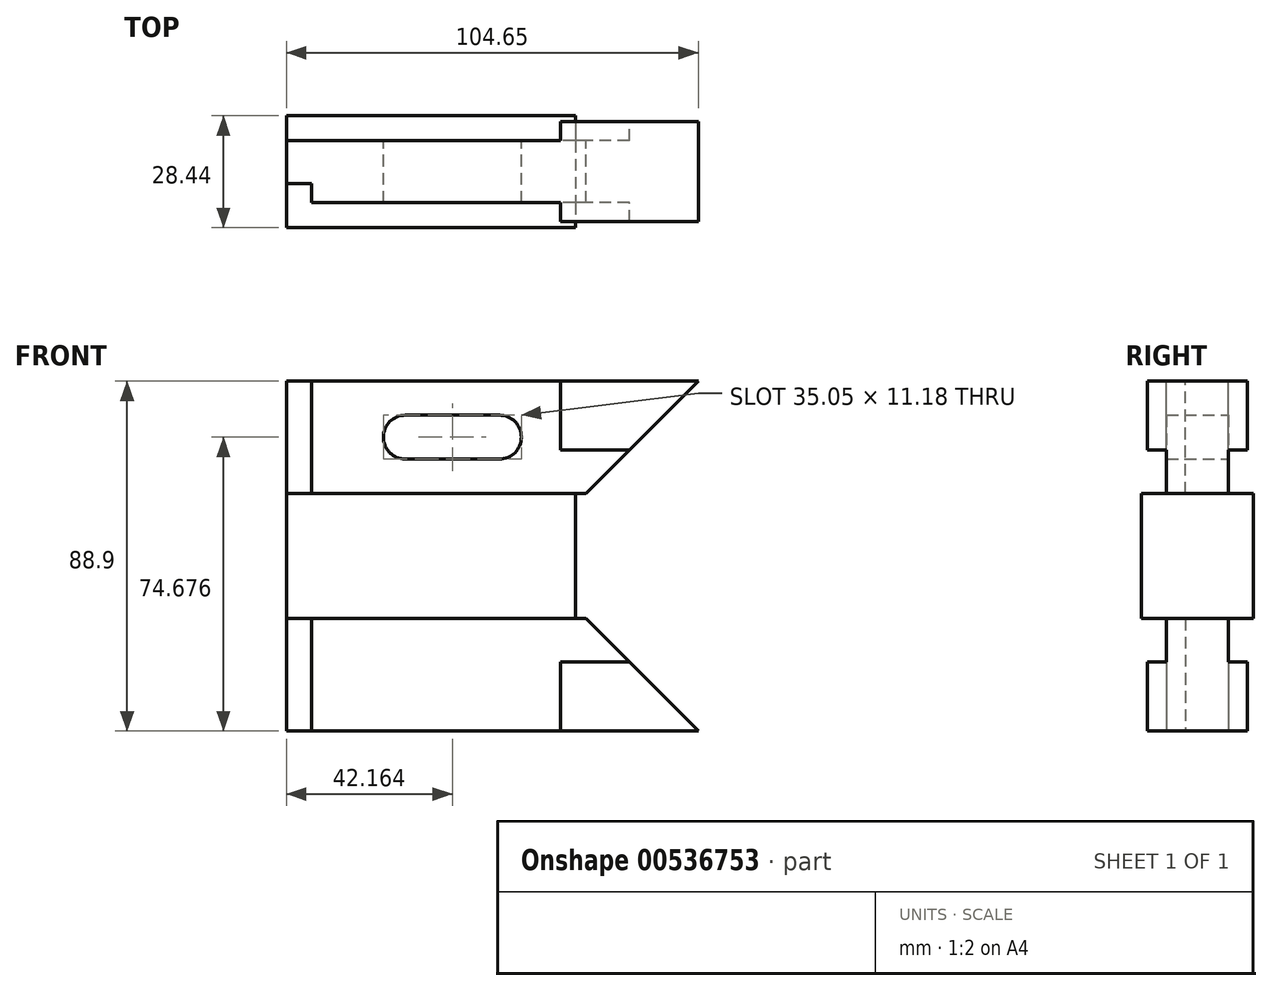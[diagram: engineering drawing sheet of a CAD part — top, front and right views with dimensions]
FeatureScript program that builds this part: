
annotation { "Feature Type Name" : "Feature", "Feature Type Description" : "" }
export const myFeature = defineFeature(function(context is Context, id is Id, definition is map)
    precondition{}
    {
        {
            var Q0;
            Q0=qCreatedBy(makeId("Right.planeOp"),FACE);
            var sketch = newSketch(context, id + "F0", { "sketchPlane" : qUnion([Q0])});
            skLineSegment(sketch, "E0.bottom", {"start": v(14.22, 15.88) * mm, "end": v(-14.22, 15.87) * mm});
            skLineSegment(sketch, "E0.top", {"start": v(14.22, -15.88) * mm, "end": v(-14.22, -15.88) * mm});
            skLineSegment(sketch, "E0.left", {"start": v(14.22, 15.88) * mm, "end": v(14.22, -15.88) * mm});
            skLineSegment(sketch, "E0.right", {"start": v(-14.22, 15.87) * mm, "end": v(-14.22, -15.88) * mm});
            skPoint(sketch, "E0.middle", {"position": v(0, 0) * mm});
            skSolve(sketch);
        }
        {
            var Q0;
            Q0=makeQuery(id+"F0.imprint","IMPRINT",FACE,{"disambiguationData":[TD([[makeQuery(id+"F0.imprint","IMPRINT",EDGE,{"derivedFrom":sQuery(id+"F0.wireOp",EDGE,"E0.bottom")}),1.0]])]});
            extrude(context, id + "F1", {"entities" : qUnion([Q0]), "depth" : 73.4 * mm, "offsetDistance" : 25.4 * mm});
        }
        {
            var Q0;
            Q0=qCreatedBy(makeId("Front.planeOp"),FACE);
            var sketch = newSketch(context, id + "F2", { "sketchPlane" : qUnion([Q0])});
            skLineSegment(sketch, "E1.0", {"start": v(73.4, 15.87) * mm, "end": v(0, 15.87) * mm});
            skLineSegment(sketch, "E2", {"start": v(0, 15.87) * mm, "end": v(0, 44.45) * mm});
            skLineSegment(sketch, "E3", {"start": v(0, 44.45) * mm, "end": v(104.65, 44.45) * mm});
            skLineSegment(sketch, "E4", {"start": v(104.65, 44.45) * mm, "end": v(76.07, 15.87) * mm});
            skLineSegment(sketch, "E5", {"start": v(76.07, 15.88) * mm, "end": v(0, 15.88) * mm});
            skArc(sketch, "E6", {"start": v(30.23, 35.81) * mm, "mid": v(24.64, 30.23) * mm, "end": v(30.23, 24.64) * mm});
            skArc(sketch, "E7", {"start": v(54.1, 24.64) * mm, "mid": v(59.7, 30.23) * mm, "end": v(54.1, 35.81) * mm});
            skLineSegment(sketch, "E8", {"start": v(30.23, 35.81) * mm, "end": v(54.1, 35.81) * mm});
            skLineSegment(sketch, "E9", {"start": v(30.23, 24.64) * mm, "end": v(54.1, 24.64) * mm});
            skLineSegment(sketch, "E10.MirrorCS", {"start": v(73.4, -15.87) * mm, "end": v(0, -15.87) * mm});
            skArc(sketch, "E11.MirrorCS", {"start": v(54.1, -24.64) * mm, "mid": v(59.7, -30.23) * mm, "end": v(54.1, -35.81) * mm});
            skLineSegment(sketch, "E12.MirrorCS", {"start": v(104.65, -44.45) * mm, "end": v(76.07, -15.87) * mm});
            skLineSegment(sketch, "E13.MirrorCS", {"start": v(0, -44.45) * mm, "end": v(104.65, -44.45) * mm});
            skArc(sketch, "E14.MirrorCS", {"start": v(30.23, -35.81) * mm, "mid": v(24.64, -30.23) * mm, "end": v(30.23, -24.64) * mm});
            skLineSegment(sketch, "E15.MirrorCS", {"start": v(30.23, -35.81) * mm, "end": v(54.1, -35.81) * mm});
            skLineSegment(sketch, "E16.MirrorCS", {"start": v(76.07, -15.88) * mm, "end": v(0, -15.88) * mm});
            skLineSegment(sketch, "E17.MirrorCS", {"start": v(30.23, -24.64) * mm, "end": v(54.1, -24.64) * mm});
            skLineSegment(sketch, "E18.MirrorCS", {"start": v(0, -15.87) * mm, "end": v(0, -44.45) * mm});
            skSolve(sketch);
        }
        {
            var Q0;
            {var subQ3=sQuery(id+"F2.wireOp",EDGE,"E2");Q0=makeQuery(id+"F2.imprint","IMPRINT",FACE,{"disambiguationData":[TD([[makeQuery(id+"F2.imprint","IMPRINT",EDGE,{"derivedFrom":subQ3}),-1.0]])]});}
            var Q1;
            Q1=makeQuery(id+"F2.imprint","IMPRINT",FACE,{"disambiguationData":[TD([[makeQuery(id+"F2.imprint","IMPRINT",EDGE,{"derivedFrom":sQuery(id+"F2.wireOp",EDGE,"E11.MirrorCS")}),1.0]])]});
            extrude(context, id + "F3", {"entities" : qUnion([Q0, Q1]), "operationType" : NewBodyOperationType.ADD, "endBound" : BoundingType.SYMMETRIC, "depth" : 15.75 * mm, "offsetDistance" : 25.4 * mm});
        }
        {
            var Q0;
            Q0=makeQuery(id+"F3.opExtrude","SWEPT_FACE",FACE,{"disambiguationData":[OSD([sQuery(id+"F2.wireOp",EDGE,"E3")])]});
            var sketch = newSketch(context, id + "F4", { "sketchPlane" : qUnion([Q0])});
            skLineSegment(sketch, "E19.bottom", {"start": v(0, -3.05) * mm, "end": v(6.35, -3.05) * mm});
            skLineSegment(sketch, "E19.right", {"start": v(6.35, -3.05) * mm, "end": v(6.35, -7.87) * mm});
            skSolve(sketch);
        }
        {
            var Q0;
            {var subQ0=sQuery(id+"F4.wireOp",EDGE,"E19.bottom");Q0=makeQuery(id+"F4.imprint","IMPRINT",FACE,{"disambiguationData":[TD([[makeQuery(id+"F4.imprint","IMPRINT",EDGE,{"derivedFrom":subQ0}),-1.0]])]});}
            extrude(context, id + "F5", {"entities" : qUnion([Q0]), "operationType" : NewBodyOperationType.REMOVE, "oppositeDirection" : true, "depth" : 28.57 * mm, "offsetDistance" : 25.4 * mm});
        }
        {
            var Q0;
            Q0=qCreatedBy(makeId("Front.planeOp"),FACE);
            var sketch = newSketch(context, id + "F6", { "sketchPlane" : qUnion([Q0])});
            skLineSegment(sketch, "E20.0", {"start": v(6.35, 44.45) * mm, "end": v(104.65, 44.45) * mm});
            skLineSegment(sketch, "E21.0", {"start": v(104.65, 44.45) * mm, "end": v(76.07, 15.87) * mm});
            skLineSegment(sketch, "E22", {"start": v(69.6, 44.45) * mm, "end": v(69.6, 26.92) * mm});
            skLineSegment(sketch, "E23", {"start": v(69.6, 26.92) * mm, "end": v(87.12, 26.92) * mm});
            skSolve(sketch);
        }
        {
            var Q0;
            {var subQ3=sQuery(id+"F6.wireOp",EDGE,"E22");Q0=makeQuery(id+"F6.imprint","IMPRINT",FACE,{"disambiguationData":[TD([[makeQuery(id+"F6.imprint","IMPRINT",EDGE,{"derivedFrom":subQ3}),1.0]])]});}
            extrude(context, id + "F7", {"entities" : qUnion([Q0]), "operationType" : NewBodyOperationType.ADD, "endBound" : BoundingType.SYMMETRIC, "depth" : 25.4 * mm, "offsetDistance" : 25.4 * mm});
        }
        {
            var Q0;
            Q0=makeQuery(id+"F1.opExtrude","SWEPT_BODY",BODY,{"disambiguationData":[OSD([sQuery(id+"F0.wireOp",EDGE,"E0.bottom"),sQuery(id+"F0.wireOp",EDGE,"E0.top"),sQuery(id+"F0.wireOp",EDGE,"E0.left"),sQuery(id+"F0.wireOp",EDGE,"E0.right")])]});
            var Q1;
            Q1=qCreatedBy(makeId("Top.planeOp"),FACE);
            mirror(context, id + "F8", {"operationType" : NewBodyOperationType.ADD, "entities" : qUnion([Q0]), "mirrorPlane" : qUnion([Q1])});
        }
    });
